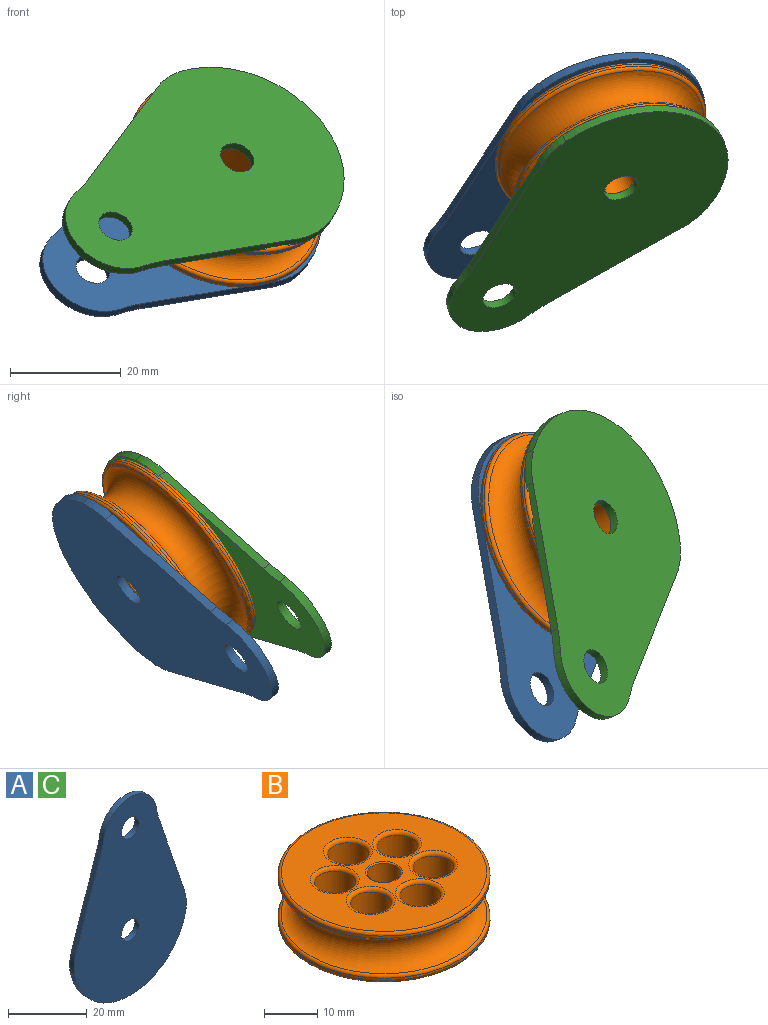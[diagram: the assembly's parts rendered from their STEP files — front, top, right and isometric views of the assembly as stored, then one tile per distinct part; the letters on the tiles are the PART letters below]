
ASSEMBLY  parts=3 mates=3
PART A: 12 faces, bbox 40.3x1.6x61.6 mm
  f0: plane 26.55x9.03mm, normal (0.95,0,0.32), area 44.5mm2, adj f1,f9,f10,f11
  f1: cylinder r=25.4mm len=4.2mm, axis (0,-1,0), area 6.9mm2, adj f0,f2,f10,f11
  f2: cylinder r=9.53mm len=18.82mm, axis (0,-1,0), area 42.8mm2, adj f1,f3,f10,f11
  f3: cylinder r=25.4mm len=4.2mm, axis (0,-1,0), area 6.9mm2, adj f2,f4,f10,f11
  f4: plane 26.55x9.03mm, normal (-0.95,0,0.32), area 44.5mm2, adj f3,f5,f10,f11
  f5: cylinder r=12.7mm len=6.76mm, axis (0,-1,0), area 10.9mm2, adj f4,f6,f10,f11
  f6: cylinder r=20.32mm len=39.73mm, axis (0,-1,0), area 87.7mm2, adj f5,f9,f10,f11
  f7: cylinder r=3.17mm len=6.35mm, axis (0,-1,0), area 31.7mm2, adj f10,f11
  f8: cylinder r=3.17mm len=6.35mm, axis (0,-1,0), area 31.7mm2, adj f10,f11
  f9: cylinder r=12.7mm len=6.76mm, axis (0,-1,0), area 10.9mm2, adj f0,f6,f10,f11
  f10: plane 61.6x40.3mm, normal (0,-1,0), area 1674.6mm2, adj f0,f1,f2,f3,f4,f5,f6,f7
  f11: plane 61.6x40.3mm, normal (0,1,0), area 1674.6mm2, adj f0,f1,f2,f3,f4,f5,f6,f7
PART B: 30 faces, bbox 43x43x11.4 mm
  f0: torus R=19.84mm, axis (0,0,-1), area 1221.5mm2, adj f5,f8
  f1: cylinder r=19.84mm len=39.69mm, axis (0,0,-1), area 64.9mm2, adj f5,f6
  f2: plane 38.42x38.42mm, normal (0,0,1), area 728.1mm2, adj f6,f11,f24,f25,f26,f27,f28,f29
  f3: plane 38.42x38.42mm, normal (0,0,-1), area 728.1mm2, adj f7,f10,f18,f19,f20,f21,f22,f23
  f4: cylinder r=19.84mm len=39.69mm, axis (0,0,-1), area 64.9mm2, adj f7,f8
  f5: torus R=19.21mm, axis (0,0,1), area 112.3mm2, adj f0,f1
  f6: torus R=19.21mm, axis (0,0,-1), area 122.9mm2, adj f1,f2
  f7: torus R=19.21mm, axis (0,0,-1), area 122.9mm2, adj f3,f4
  f8: torus R=19.21mm, axis (0,0,1), area 112.3mm2, adj f0,f4
  f9: cylinder r=3.17mm len=10.92mm, axis (0,0,1), area 217.9mm2, adj f10,f11
  f10: torus R=3.43mm, axis (0,0,-1), area 8.2mm2, adj f3,f9
  f11: torus R=3.43mm, axis (0,0,-1), area 8.2mm2, adj f2,f9
  f12: cylinder r=3.81mm len=9.91mm, axis (0,0,1), area 237.1mm2, adj f23,f29
  f13: cylinder r=3.81mm len=9.91mm, axis (0,0,1), area 237.1mm2, adj f22,f24
  f14: cylinder r=3.81mm len=9.91mm, axis (0,0,1), area 237.1mm2, adj f21,f25
  f15: cylinder r=3.81mm len=9.91mm, axis (0,0,1), area 237.1mm2, adj f20,f26
  f16: cylinder r=3.81mm len=9.91mm, axis (0,0,1), area 237.1mm2, adj f19,f27
  f17: cylinder r=3.81mm len=9.91mm, axis (0,0,1), area 237.1mm2, adj f18,f28
  f18: torus R=4.57mm, axis (0,0,-1), area 30.7mm2, adj f3,f17
  f19: torus R=4.57mm, axis (0,0,-1), area 30.7mm2, adj f3,f16
  f20: torus R=4.57mm, axis (0,0,-1), area 30.7mm2, adj f3,f15
  f21: torus R=4.57mm, axis (0,0,-1), area 30.7mm2, adj f3,f14
  f22: torus R=4.57mm, axis (0,0,-1), area 30.7mm2, adj f3,f13
  f23: torus R=4.57mm, axis (0,0,-1), area 30.7mm2, adj f3,f12
  f24: torus R=4.57mm, axis (0,0,-1), area 30.7mm2, adj f2,f13
  f25: torus R=4.57mm, axis (0,0,-1), area 30.7mm2, adj f2,f14
  f26: torus R=4.57mm, axis (0,0,-1), area 30.7mm2, adj f2,f15
  f27: torus R=4.57mm, axis (0,0,-1), area 30.7mm2, adj f2,f16
  f28: torus R=4.57mm, axis (0,0,-1), area 30.7mm2, adj f2,f17
  f29: torus R=4.57mm, axis (0,0,-1), area 30.7mm2, adj f2,f12
PART C: same geometry as A
PLACE A rot(axis=(0.89,0.01,-0.45),137.5deg) t=(-27.04,-34.25,-14.09)mm
PLACE B rot(axis=(0.35,-0.33,0.88),137.5deg) t=(2.46,-15.98,5.73)mm
PLACE C rot(axis=(0.89,0.01,-0.45),137.5deg) t=(-22.95,-43.8,-6.36)mm
MATE cylindrical C.f8 <-> A.f8  axis (-0.32,0.74,-0.6) through (-17.79,-39.24,-3.46)mm
MATE revolute B.f0 <-> A.f6  axis (-0.32,0.74,-0.6) through (0.59,-11.62,2.2)mm
MATE revolute B.f9 <-> C.f7  axis (0.32,-0.74,0.6) through (4.12,-19.86,8.87)mm
